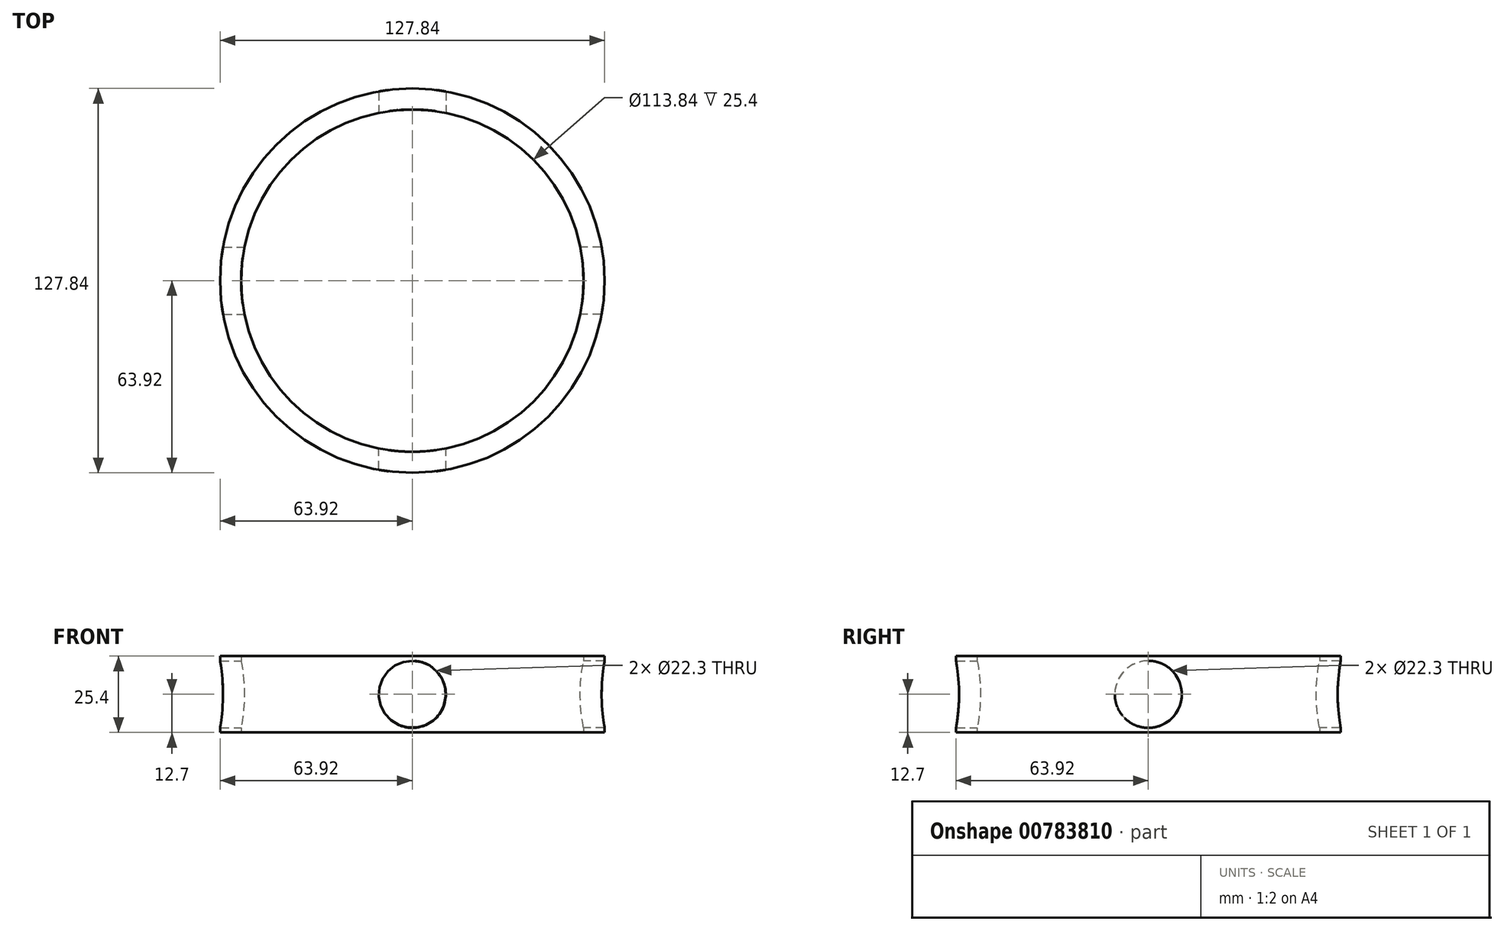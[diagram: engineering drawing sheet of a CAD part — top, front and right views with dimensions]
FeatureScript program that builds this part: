
annotation { "Feature Type Name" : "Feature", "Feature Type Description" : "" }
export const myFeature = defineFeature(function(context is Context, id is Id, definition is map)
    precondition{}
    {
        {
            var Q0;
            Q0=qCreatedBy(makeId("Top.planeOp"),FACE);
            var sketch = newSketch(context, id + "F0", { "sketchPlane" : qUnion([Q0])});
            skCircle(sketch, "E0", {"center": v(0, 0) * mm, "radius": 63.92 * mm});
            skCircle(sketch, "E1", {"center": v(0, 0) * mm, "radius": 56.92 * mm});
            skSolve(sketch);
        }
        {
            var Q0;
            Q0=makeQuery(id+"F0.imprint","IMPRINT",FACE,{"disambiguationData":[TD([[makeQuery(id+"F0.imprint","IMPRINT",EDGE,{"derivedFrom":sQuery(id+"F0.wireOp",EDGE,"E0")}),1.0]])]});
            extrude(context, id + "F1", {"entities" : qUnion([Q0]), "depth" : 25.4 * mm, "offsetDistance" : 25.4 * mm});
        }
        {
            var Q0;
            Q0=qCreatedBy(makeId("Front.planeOp"),FACE);
            var sketch = newSketch(context, id + "F2", { "sketchPlane" : qUnion([Q0])});
            skCircle(sketch, "E2", {"center": v(0, 12.7) * mm, "radius": 11.15 * mm});
            skSolve(sketch);
        }
        {
            var Q0;
            Q0=makeQuery(id+"F2.imprint","IMPRINT",FACE,{"disambiguationData":[TD([[makeQuery(id+"F2.imprint","IMPRINT",EDGE,{"derivedFrom":sQuery(id+"F2.wireOp",EDGE,"E2")}),1.0]])]});
            extrude(context, id + "F3", {"entities" : qUnion([Q0]), "operationType" : NewBodyOperationType.REMOVE, "oppositeDirection" : true, "depth" : -76.2 * mm, "offsetDistance" : 25.4 * mm});
        }
        {
            var Q0;
            Q0=qCreatedBy(makeId("Front.planeOp"),FACE);
            var sketch = newSketch(context, id + "F4", { "sketchPlane" : qUnion([Q0])});
            skCircle(sketch, "E3", {"center": v(0, 12.7) * mm, "radius": 11.15 * mm});
            skSolve(sketch);
        }
        {
            var Q0;
            Q0=makeQuery(id+"F4.imprint","IMPRINT",FACE,{"disambiguationData":[TD([[makeQuery(id+"F4.imprint","IMPRINT",EDGE,{"derivedFrom":sQuery(id+"F4.wireOp",EDGE,"E3")}),1.0]])]});
            extrude(context, id + "F5", {"entities" : qUnion([Q0]), "operationType" : NewBodyOperationType.REMOVE, "oppositeDirection" : true, "depth" : 76.2 * mm, "offsetDistance" : 25.4 * mm});
        }
        {
            var Q0;
            Q0=qCreatedBy(makeId("Right.planeOp"),FACE);
            var sketch = newSketch(context, id + "F6", { "sketchPlane" : qUnion([Q0])});
            skCircle(sketch, "E4", {"center": v(0, 12.7) * mm, "radius": 11.15 * mm});
            skSolve(sketch);
        }
        {
            var Q0;
            Q0=makeQuery(id+"F6.imprint","IMPRINT",FACE,{"disambiguationData":[TD([[makeQuery(id+"F6.imprint","IMPRINT",EDGE,{"derivedFrom":sQuery(id+"F6.wireOp",EDGE,"E4")}),1.0]])]});
            extrude(context, id + "F7", {"entities" : qUnion([Q0]), "operationType" : NewBodyOperationType.REMOVE, "oppositeDirection" : true, "depth" : 76.2 * mm, "offsetDistance" : 25.4 * mm});
        }
        {
            var Q0;
            Q0=qCreatedBy(makeId("Right.planeOp"),FACE);
            var sketch = newSketch(context, id + "F8", { "sketchPlane" : qUnion([Q0])});
            skCircle(sketch, "E5", {"center": v(0, 12.7) * mm, "radius": 11.15 * mm});
            skSolve(sketch);
        }
        {
            var Q0;
            Q0=makeQuery(id+"F8.imprint","IMPRINT",FACE,{"disambiguationData":[TD([[makeQuery(id+"F8.imprint","IMPRINT",EDGE,{"derivedFrom":sQuery(id+"F8.wireOp",EDGE,"E5")}),1.0]])]});
            extrude(context, id + "F9", {"entities" : qUnion([Q0]), "operationType" : NewBodyOperationType.REMOVE, "oppositeDirection" : true, "depth" : -76.2 * mm, "offsetDistance" : 25.4 * mm});
        }
    });
